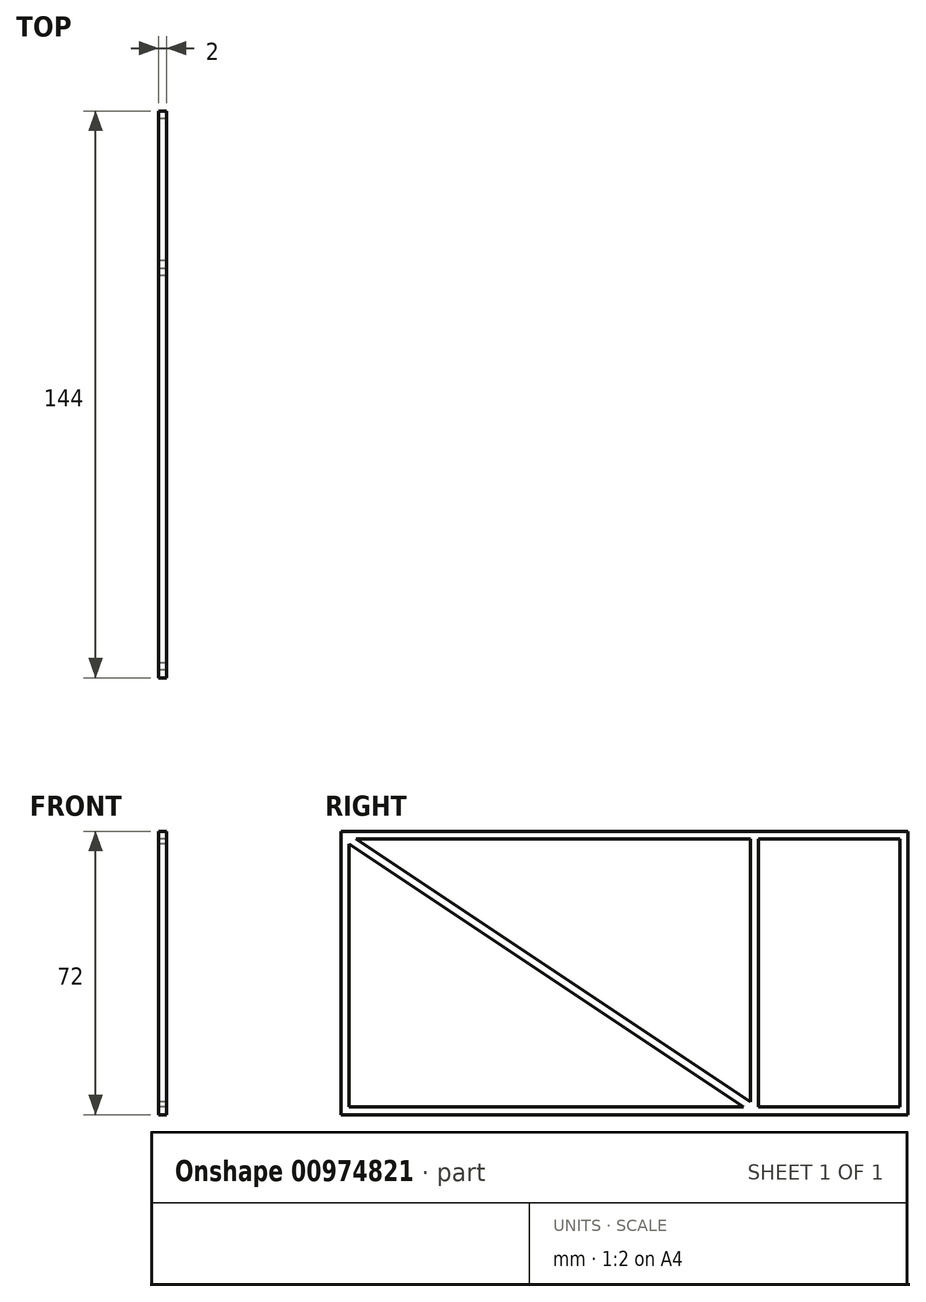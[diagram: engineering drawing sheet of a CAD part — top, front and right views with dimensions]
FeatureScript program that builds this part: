
annotation { "Feature Type Name" : "Feature", "Feature Type Description" : "" }
export const myFeature = defineFeature(function(context is Context, id is Id, definition is map)
    precondition{}
    {
        {
            var Q0;
            Q0=qCreatedBy(makeId("Right.planeOp"),FACE);
            var sketch = newSketch(context, id + "F0", { "sketchPlane" : qUnion([Q0])});
            skLineSegment(sketch, "E0.bottom", {"start": v(0, 0) * mm, "end": v(144, 0) * mm});
            skLineSegment(sketch, "E0.top", {"start": v(0, 72) * mm, "end": v(144, 72) * mm});
            skLineSegment(sketch, "E0.left", {"start": v(0, 0) * mm, "end": v(0, 72) * mm});
            skLineSegment(sketch, "E0.right", {"start": v(144, 0) * mm, "end": v(144, 72) * mm});
            skLineSegment(sketch, "E1", {"start": v(2, 68.8) * mm, "end": v(2, 2) * mm});
            skLineSegment(sketch, "E2", {"start": v(2, 2) * mm, "end": v(102.2, 2) * mm});
            skLineSegment(sketch, "E3", {"start": v(102.2, 2) * mm, "end": v(2, 68.8) * mm});
            skLineSegment(sketch, "E4", {"start": v(104, 3.2) * mm, "end": v(104, 70) * mm});
            skLineSegment(sketch, "E5", {"start": v(104, 70) * mm, "end": v(3.8, 70) * mm});
            skLineSegment(sketch, "E6", {"start": v(3.8, 70) * mm, "end": v(104, 3.2) * mm});
            skLineSegment(sketch, "E7.bottom", {"start": v(142, 70) * mm, "end": v(106, 70) * mm});
            skLineSegment(sketch, "E7.top", {"start": v(142, 2) * mm, "end": v(106, 2) * mm});
            skLineSegment(sketch, "E7.left", {"start": v(142, 70) * mm, "end": v(142, 2) * mm});
            skLineSegment(sketch, "E7.right", {"start": v(106, 70) * mm, "end": v(106, 2) * mm});
            skLineSegment(sketch, "E8.bottom", {"start": v(104, 70) * mm, "end": v(2, 70) * mm, "construction": true});
            skLineSegment(sketch, "E8.top", {"start": v(104, 2) * mm, "end": v(2, 2) * mm, "construction": true});
            skLineSegment(sketch, "E8.left", {"start": v(104, 70) * mm, "end": v(104, 2) * mm, "construction": true});
            skLineSegment(sketch, "E8.right", {"start": v(2, 70) * mm, "end": v(2, 2) * mm, "construction": true});
            skLineSegment(sketch, "E9", {"start": v(2, 70) * mm, "end": v(104, 2) * mm, "construction": true});
            skSolve(sketch);
        }
        {
            var Q0;
            Q0=qSketchRegion(id+"F0",true);
            extrude(context, id + "F1", {"entities" : qUnion([Q0]), "depth" : 2 * mm, "offsetDistance" : 25 * mm});
        }
    });
